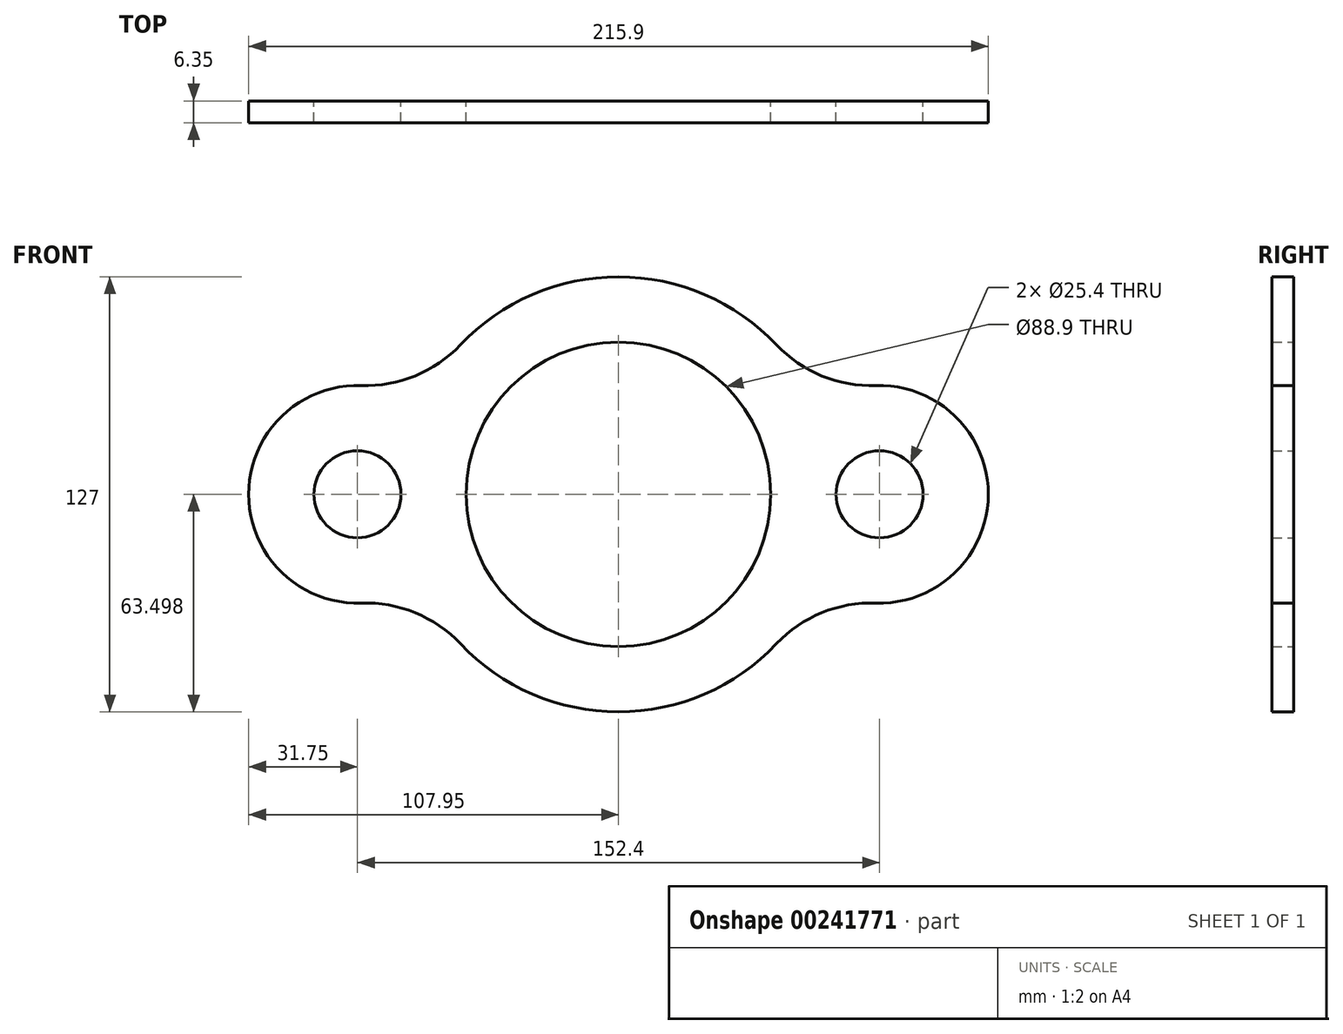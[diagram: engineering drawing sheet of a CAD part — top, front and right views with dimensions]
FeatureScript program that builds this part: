
annotation { "Feature Type Name" : "Feature", "Feature Type Description" : "" }
export const myFeature = defineFeature(function(context is Context, id is Id, definition is map)
    precondition{}
    {
        {
            var Q0;
            Q0=qCreatedBy(makeId("Front.planeOp"),FACE);
            var sketch = newSketch(context, id + "F0", { "sketchPlane" : qUnion([Q0])});
            skArc(sketch, "E0", {"start": v(-103.1, 113.19) * mm, "mid": v(-149.24, 133.06) * mm, "end": v(-195.38, 113.19) * mm});
            skCircle(sketch, "E1", {"center": v(-149.24, 69.56) * mm, "radius": 44.45 * mm});
            skLineSegment(sketch, "E2", {"start": v(-225.44, 69.56) * mm, "end": v(-73.04, 69.56) * mm, "construction": true});
            skArc(sketch, "E3", {"start": v(-74.12, 37.83) * mm, "mid": v(-41.3, 69.56) * mm, "end": v(-74.12, 101.29) * mm});
            skCircle(sketch, "E4", {"center": v(-73.04, 69.56) * mm, "radius": 12.7 * mm});
            skArc(sketch, "E5", {"start": v(-224.36, 101.29) * mm, "mid": v(-257.2, 69.56) * mm, "end": v(-224.36, 37.83) * mm});
            skCircle(sketch, "E6", {"center": v(-225.44, 69.56) * mm, "radius": 12.7 * mm});
            skArc(sketch, "E7.trimOffspring", {"start": v(-195.38, 25.93) * mm, "mid": v(-149.24, 6.06) * mm, "end": v(-103.1, 25.93) * mm});
            skPoint(sketch, "E8.visualSharp", {"position": v(-207.18, 95.53) * mm});
            skArc(sketch, "E8.filletArc", {"start": v(-224.36, 101.29) * mm, "mid": v(-208.59, 104.12) * mm, "end": v(-195.38, 113.19) * mm});
            skPoint(sketch, "E9.visualSharp", {"position": v(-207.18, 43.58) * mm});
            skArc(sketch, "E9.filletArc", {"start": v(-195.38, 25.93) * mm, "mid": v(-208.59, 35) * mm, "end": v(-224.36, 37.83) * mm});
            skPoint(sketch, "E10.visualSharp", {"position": v(-91.3, 43.58) * mm});
            skArc(sketch, "E10.filletArc", {"start": v(-74.12, 37.83) * mm, "mid": v(-89.9, 35) * mm, "end": v(-103.1, 25.93) * mm});
            skPoint(sketch, "E11.visualSharp", {"position": v(-91.3, 95.53) * mm});
            skArc(sketch, "E11.filletArc", {"start": v(-103.1, 113.19) * mm, "mid": v(-89.9, 104.12) * mm, "end": v(-74.12, 101.29) * mm});
            skSolve(sketch);
        }
        {
            var Q0;
            Q0 = qSketchRegion(id + "F0", true);
            extrude(context, id + "F1", {"entities" : qUnion([Q0]), "depth" : 6.35 * mm});
        }
    });
